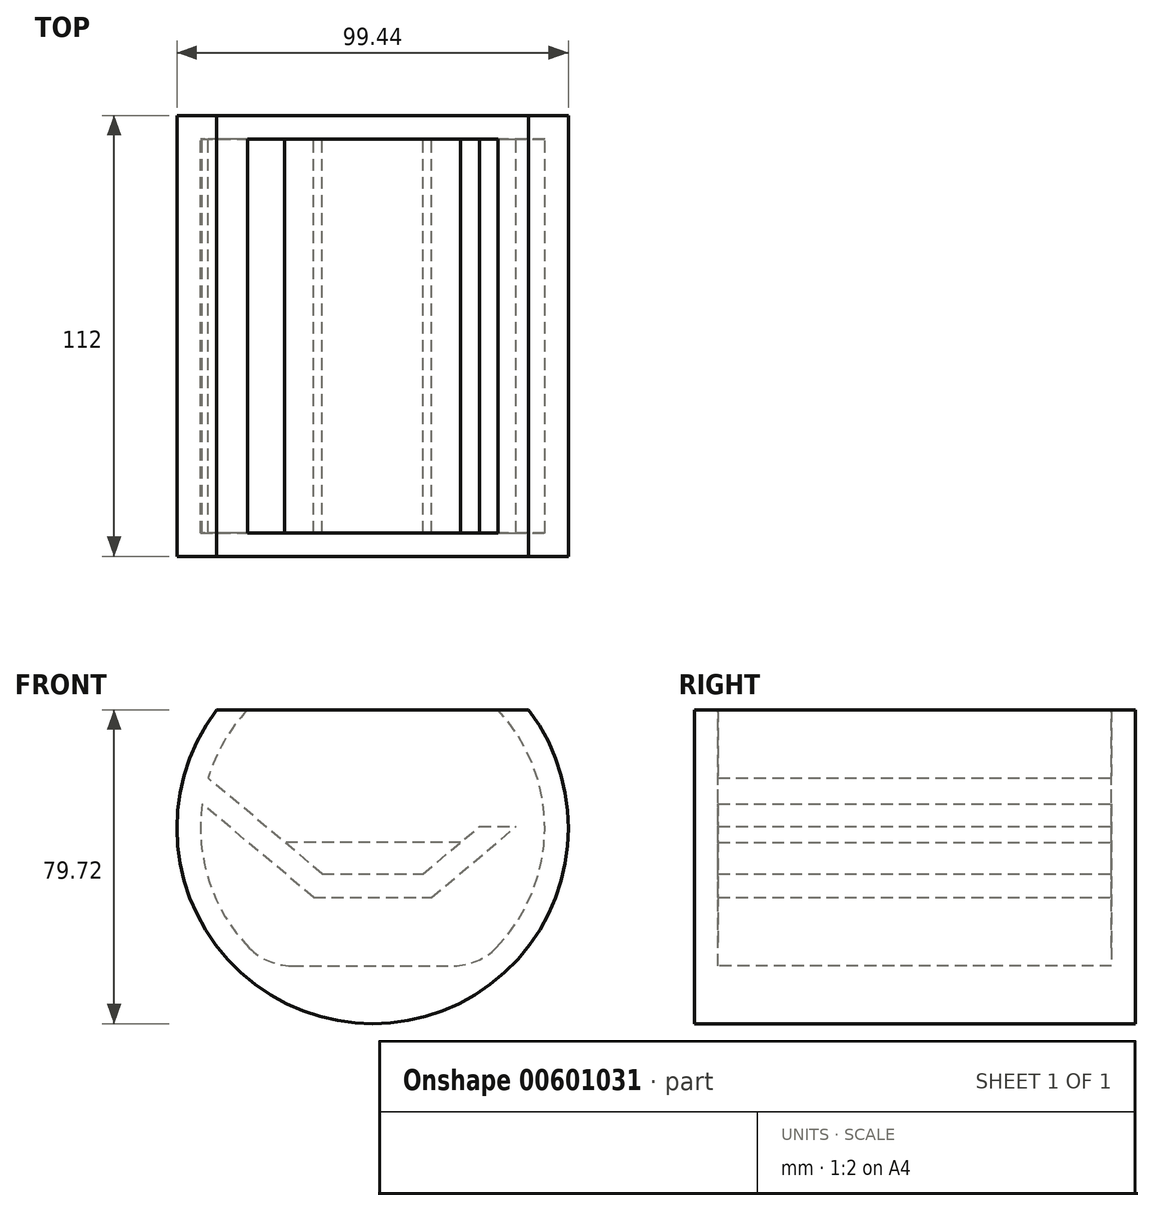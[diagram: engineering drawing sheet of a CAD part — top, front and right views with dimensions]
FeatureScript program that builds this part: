
annotation { "Feature Type Name" : "Feature", "Feature Type Description" : "" }
export const myFeature = defineFeature(function(context is Context, id is Id, definition is map)
    precondition{}
    {
        {
            var Q0;
            Q0=qCreatedBy(makeId("Front.planeOp"),FACE);
            var sketch = newSketch(context, id + "F0", { "sketchPlane" : qUnion([Q0])});
            skArc(sketch, "E0", {"start": v(-43.3, 6.1) * mm, "mid": v(-40.36, -16.8) * mm, "end": v(-26.2, -35) * mm});
            skArc(sketch, "E1", {"start": v(-39.64, 30) * mm, "mid": v(0, -49.72) * mm, "end": v(39.64, 30) * mm});
            skLineSegment(sketch, "E2", {"start": v(-12.82, -11.65) * mm, "end": v(-41.83, 12.7) * mm});
            skLineSegment(sketch, "E3", {"start": v(-15, -17.65) * mm, "end": v(-43.3, 6.1) * mm});
            skLineSegment(sketch, "E4", {"start": v(12.82, -11.65) * mm, "end": v(27.12, 0.35) * mm});
            skLineSegment(sketch, "E5", {"start": v(15, -17.65) * mm, "end": v(36.45, 0.35) * mm});
            skLineSegment(sketch, "E6", {"start": v(-26.2, -35) * mm, "end": v(26.2, -35) * mm});
            skLineSegment(sketch, "E7", {"start": v(-15, -17.65) * mm, "end": v(15, -17.65) * mm});
            skPoint(sketch, "E8.orphan", {"position": v(0, -30.23) * mm});
            skArc(sketch, "E9.trimOffspring", {"start": v(26.2, -35) * mm, "mid": v(43.55, -3.76) * mm, "end": v(31.8, 30) * mm});
            skLineSegment(sketch, "E10", {"start": v(-39.64, 30) * mm, "end": v(-31.8, 30) * mm});
            skArc(sketch, "E11.trimOffspring", {"start": v(-31.8, 30) * mm, "mid": v(-37.82, 21.93) * mm, "end": v(-41.83, 12.7) * mm});
            skLineSegment(sketch, "E12.trimOffspring", {"start": v(31.8, 30) * mm, "end": v(39.64, 30) * mm});
            skLineSegment(sketch, "E13", {"start": v(-12.82, -11.65) * mm, "end": v(12.82, -11.65) * mm});
            skLineSegment(sketch, "E14", {"start": v(27.12, 0.35) * mm, "end": v(36.45, 0.35) * mm});
            skLineSegment(sketch, "E15", {"start": v(0, 0) * mm, "end": v(0, -11.65) * mm, "construction": true});
            skLineSegment(sketch, "E16", {"start": v(0, -11.65) * mm, "end": v(0, -17.65) * mm, "construction": true});
            skSolve(sketch);
        }
        {
            var Q0;
            Q0 = qSketchRegion(id + "F0", true);
            extrude(context, id + "F1", {"entities" : qUnion([Q0]), "endBound" : BoundingType.SYMMETRIC, "depth" : 100 * mm, "offsetDistance" : 25 * mm});
        }
        {
            var Q0;
            Q0=makeQuery(id+"F1.opExtrude","CAP_FACE",FACE,{"disambiguationData":[OSD([sQuery(id+"F0.wireOp",EDGE,"E0"),sQuery(id+"F0.wireOp",EDGE,"E1"),sQuery(id+"F0.wireOp",EDGE,"E2"),sQuery(id+"F0.wireOp",EDGE,"E3"),sQuery(id+"F0.wireOp",EDGE,"E4"),sQuery(id+"F0.wireOp",EDGE,"E5"),sQuery(id+"F0.wireOp",EDGE,"E6"),sQuery(id+"F0.wireOp",EDGE,"E7"),sQuery(id+"F0.wireOp",EDGE,"E9.trimOffspring"),sQuery(id+"F0.wireOp",EDGE,"E10"),sQuery(id+"F0.wireOp",EDGE,"E11.trimOffspring"),sQuery(id+"F0.wireOp",EDGE,"E12.trimOffspring"),sQuery(id+"F0.wireOp",EDGE,"E13"),sQuery(id+"F0.wireOp",EDGE,"E14")])],"isStart":false});
            var sketch = newSketch(context, id + "F2", { "sketchPlane" : qUnion([Q0])});
            skArc(sketch, "E17.0", {"start": v(-39.64, 30) * mm, "mid": v(0, -49.72) * mm, "end": v(39.64, 30) * mm});
            skLineSegment(sketch, "E18", {"start": v(-39.64, 30) * mm, "end": v(39.64, 30) * mm});
            skSolve(sketch);
        }
        {
            var Q0;
            Q0 = qSketchRegion(id + "F2", true);
            extrude(context, id + "F3", {"entities" : qUnion([Q0]), "operationType" : NewBodyOperationType.ADD, "depth" : 6 * mm, "offsetDistance" : 25 * mm});
        }
        {
            var Q0;
            Q0=makeQuery(id+"F1.opExtrude","CAP_FACE",FACE,{"disambiguationData":[OSD([sQuery(id+"F0.wireOp",EDGE,"E0"),sQuery(id+"F0.wireOp",EDGE,"E1"),sQuery(id+"F0.wireOp",EDGE,"E2"),sQuery(id+"F0.wireOp",EDGE,"E3"),sQuery(id+"F0.wireOp",EDGE,"E4"),sQuery(id+"F0.wireOp",EDGE,"E5"),sQuery(id+"F0.wireOp",EDGE,"E6"),sQuery(id+"F0.wireOp",EDGE,"E7"),sQuery(id+"F0.wireOp",EDGE,"E9.trimOffspring"),sQuery(id+"F0.wireOp",EDGE,"E10"),sQuery(id+"F0.wireOp",EDGE,"E11.trimOffspring"),sQuery(id+"F0.wireOp",EDGE,"E12.trimOffspring"),sQuery(id+"F0.wireOp",EDGE,"E13"),sQuery(id+"F0.wireOp",EDGE,"E14")])],"isStart":true});
            var sketch = newSketch(context, id + "F4", { "sketchPlane" : qUnion([Q0])});
            skArc(sketch, "E19.0", {"start": v(39.64, 30) * mm, "mid": v(0, -49.72) * mm, "end": v(-39.64, 30) * mm});
            skLineSegment(sketch, "E19.1", {"start": v(39.64, 30) * mm, "end": v(-39.64, 30) * mm});
            skSolve(sketch);
        }
        {
            var Q0;
            Q0 = qSketchRegion(id + "F4", true);
            extrude(context, id + "F5", {"entities" : qUnion([Q0]), "operationType" : NewBodyOperationType.ADD, "depth" : 6 * mm, "offsetDistance" : 25 * mm});
        }
        {
            var Q0;
            Q0=qCreatedBy(makeId("Front.planeOp"),FACE);
            var sketch = newSketch(context, id + "F6", { "sketchPlane" : qUnion([Q0])});
            skLineSegment(sketch, "E20.0", {"start": v(12.82, -11.65) * mm, "end": v(22.35, -3.65) * mm});
            skLineSegment(sketch, "E21.0", {"start": v(-12.82, -11.65) * mm, "end": v(12.82, -11.65) * mm});
            skLineSegment(sketch, "E22.0", {"start": v(-12.82, -11.65) * mm, "end": v(-22.35, -3.65) * mm});
            skLineSegment(sketch, "E23", {"start": v(22.35, -3.65) * mm, "end": v(-22.35, -3.65) * mm});
            skPoint(sketch, "E24.orphan", {"position": v(27.12, 0.35) * mm});
            skPoint(sketch, "E25.orphan", {"position": v(-41.83, 12.7) * mm});
            skSolve(sketch);
        }
        {
            var Q0;
            Q0 = qSketchRegion(id + "F6", true);
            extrude(context, id + "F7", {"entities" : qUnion([Q0]), "endBound" : BoundingType.SYMMETRIC, "depth" : 100 * mm, "offsetDistance" : 25 * mm});
        }
        {
            var Q0;
            Q0=makeQuery(id+"F1.opExtrude","SWEPT_EDGE",EDGE,{"disambiguationData":[OSD([sQuery(id+"F0.wireOp",EDGE,"E0"),sQuery(id+"F0.wireOp",EDGE,"E6")])]});
            var Q1;
            Q1=makeQuery(id+"F1.opExtrude","SWEPT_EDGE",EDGE,{"disambiguationData":[OSD([sQuery(id+"F0.wireOp",EDGE,"E6"),sQuery(id+"F0.wireOp",EDGE,"E9.trimOffspring")])]});
            fillet(context, id + "F8", {"entities" : qUnion([Q0, Q1]), "radius" : 15 * mm, "tangentPropagation" : true, "allowEdgeOverflow" : false});
        }
    });
